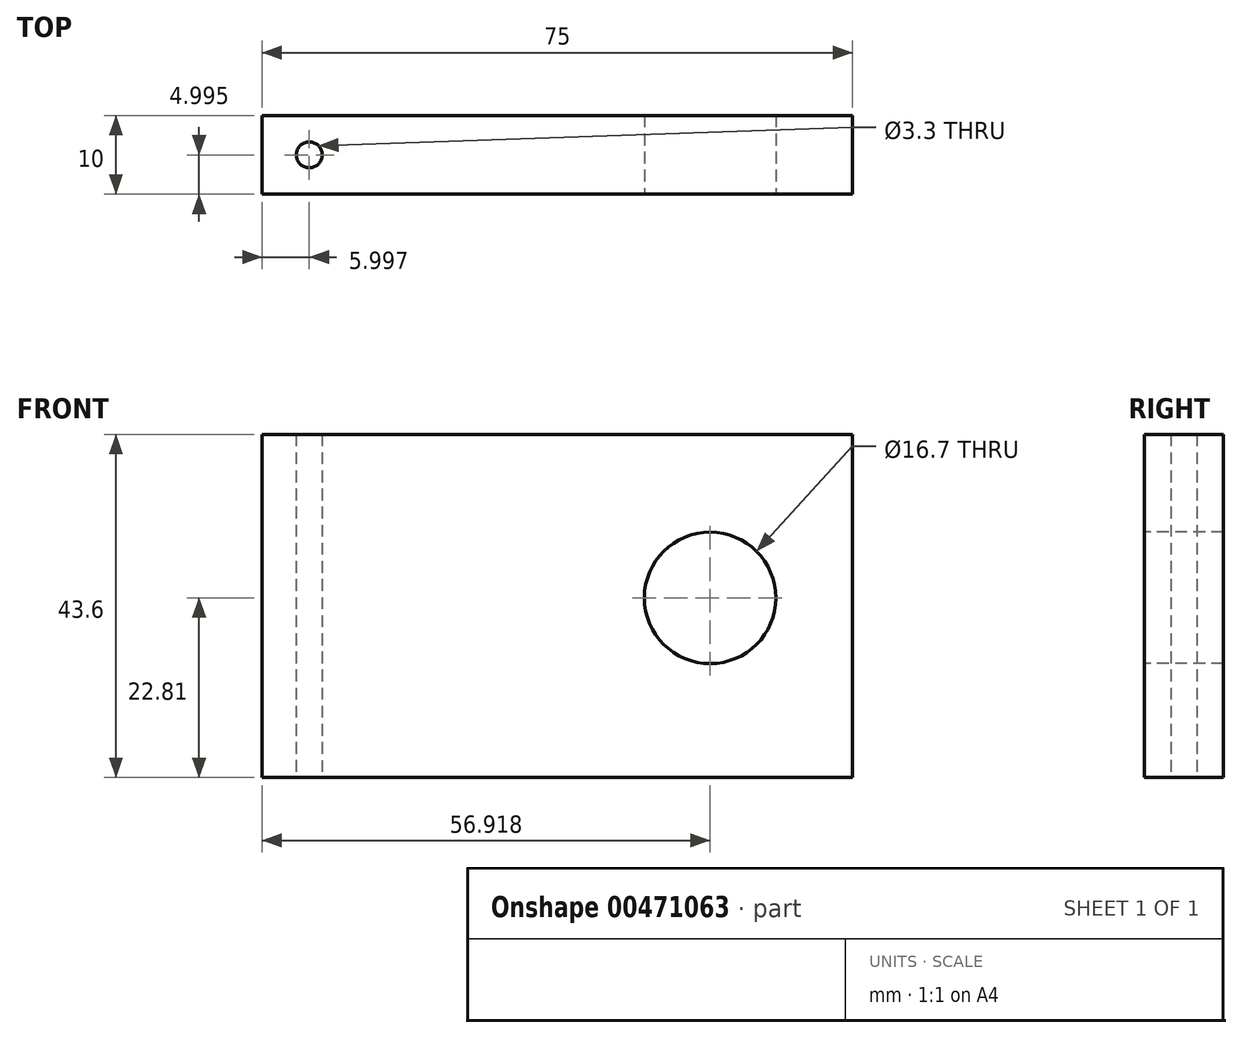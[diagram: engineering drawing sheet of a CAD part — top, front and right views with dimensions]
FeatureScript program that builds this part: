
annotation { "Feature Type Name" : "Feature", "Feature Type Description" : "" }
export const myFeature = defineFeature(function(context is Context, id is Id, definition is map)
    precondition{}
    {
        {
            var Q0;
            Q0=qCreatedBy(makeId("Top.planeOp"),FACE);
            var sketch = newSketch(context, id + "F0", { "sketchPlane" : qUnion([Q0])});
            skLineSegment(sketch, "E0", {"start": v(-73.43, 12.15) * mm, "end": v(1.57, 12.15) * mm});
            skLineSegment(sketch, "E1", {"start": v(1.57, 12.15) * mm, "end": v(1.57, 22.15) * mm});
            skLineSegment(sketch, "E2", {"start": v(1.57, 22.15) * mm, "end": v(-73.43, 22.15) * mm});
            skLineSegment(sketch, "E3", {"start": v(-73.43, 22.15) * mm, "end": v(-73.43, 12.15) * mm});
            skCircle(sketch, "E4", {"center": v(-67.43, 17.15) * mm, "radius": 1.65 * mm});
            skSolve(sketch);
        }
        {
            var Q0;
            Q0 = qSketchRegion(id + "F0", true);
            extrude(context, id + "F1", {"entities" : qUnion([Q0]), "depth" : 43.6 * mm, "offsetDistance" : 25 * mm});
        }
        {
            var Q0;
            Q0=qCreatedBy(makeId("Front.planeOp"),FACE);
            var sketch = newSketch(context, id + "F2", { "sketchPlane" : qUnion([Q0])});
            skCircle(sketch, "E5", {"center": v(-16.51, 22.8) * mm, "radius": 8.35 * mm});
            skSolve(sketch);
        }
        {
            var Q0;
            Q0=sQuery(id+"F2.wireOp",VERTEX,"E5.center");
            var Q1;
            Q1=makeQuery(id+"F1.opExtrude","SWEPT_BODY",BODY,{"disambiguationData":[OSD([sQuery(id+"F0.wireOp",EDGE,"E0"),sQuery(id+"F0.wireOp",EDGE,"E1"),sQuery(id+"F0.wireOp",EDGE,"E2"),sQuery(id+"F0.wireOp",EDGE,"E3"),sQuery(id+"F0.wireOp",EDGE,"E4")])]});
            hole(context, id + "F3", {"style" : HoleStyle.SIMPLE, "endStyle" : HoleEndStyle.THROUGH, "holeDiameter" : 16.7 * mm, "isTappedThrough" : true, "tappedDepth" : 12 * mm, "tapClearance" : 3, "locations" : qUnion([Q0]), "scope" : qUnion([Q1])});
        }
    });
